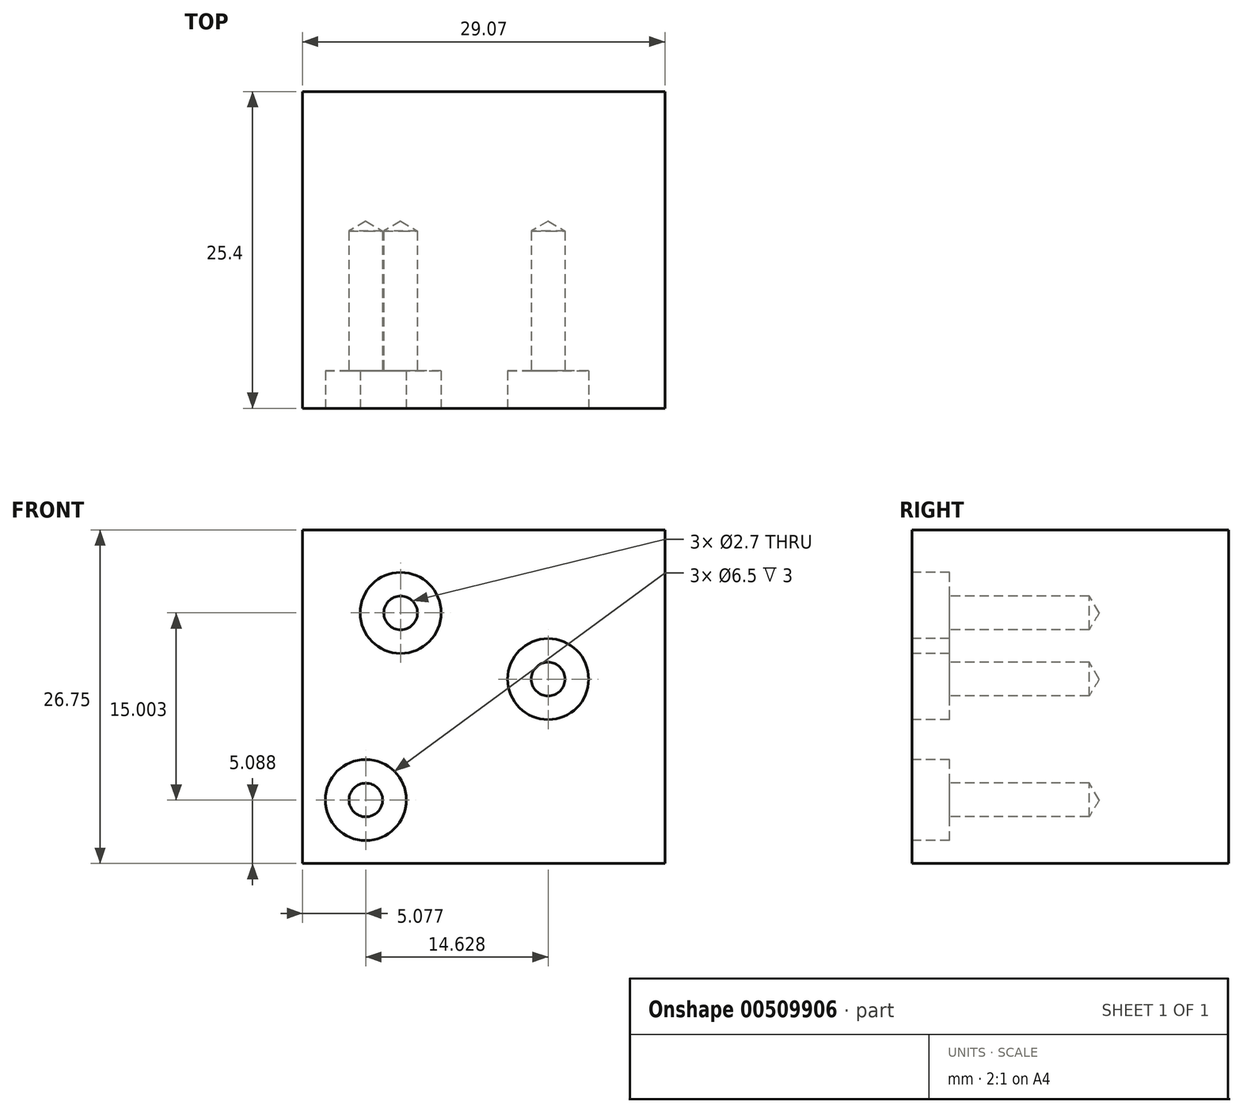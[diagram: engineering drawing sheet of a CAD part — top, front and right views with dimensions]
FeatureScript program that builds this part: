
annotation { "Feature Type Name" : "Feature", "Feature Type Description" : "" }
export const myFeature = defineFeature(function(context is Context, id is Id, definition is map)
    precondition{}
    {
        {
            var Q0;
            Q0=qCreatedBy(makeId("Front.planeOp"),FACE);
            var sketch = newSketch(context, id + "F0", { "sketchPlane" : qUnion([Q0])});
            skLineSegment(sketch, "E0.bottom", {"start": v(-46.75, 46.52) * mm, "end": v(-17.68, 46.52) * mm});
            skLineSegment(sketch, "E0.top", {"start": v(-46.75, 19.77) * mm, "end": v(-17.68, 19.77) * mm});
            skLineSegment(sketch, "E0.left", {"start": v(-46.75, 46.52) * mm, "end": v(-46.75, 19.77) * mm});
            skLineSegment(sketch, "E0.right", {"start": v(-17.68, 46.52) * mm, "end": v(-17.68, 19.77) * mm});
            skPoint(sketch, "E1", {"position": v(-38.88, 39.86) * mm});
            skPoint(sketch, "E2", {"position": v(-41.67, 24.86) * mm});
            skPoint(sketch, "E3", {"position": v(-27.04, 34.55) * mm});
            skSolve(sketch);
        }
        {
            var Q0;
            Q0=makeQuery(id+"F0.imprint","IMPRINT",FACE,{"disambiguationData":[TD([[makeQuery(id+"F0.imprint","IMPRINT",EDGE,{"derivedFrom":sQuery(id+"F0.wireOp",EDGE,"E0.bottom")}),-1.0]])]});
            extrude(context, id + "F1", {"entities" : qUnion([Q0]), "oppositeDirection" : true, "depth" : 25.4 * mm, "offsetDistance" : 25.4 * mm});
        }
        {
            var Q0;
            Q0=sQuery(id+"F0.wireOp",VERTEX,"E3");
            var Q1;
            Q1=sQuery(id+"F0.wireOp",VERTEX,"E2");
            var Q2;
            Q2=sQuery(id+"F0.wireOp",VERTEX,"E1");
            var Q3;
            Q3=makeQuery(id+"F1.opExtrude","SWEPT_BODY",BODY,{"disambiguationData":[OSD([sQuery(id+"F0.wireOp",EDGE,"E0.bottom"),sQuery(id+"F0.wireOp",EDGE,"E0.top"),sQuery(id+"F0.wireOp",EDGE,"E0.left"),sQuery(id+"F0.wireOp",EDGE,"E0.right")])]});
            hole(context, id + "F2", {"style" : HoleStyle.C_BORE, "endStyle" : HoleEndStyle.BLIND, "standardTappedOrClearance" : lookupTablePath({ "standard" : "ISO", "engagement" : "50%", "pitch" : "0.5 mm", "size" : "M3", "type" : "Tapped" }), "standardBlindInLast" : lookupTablePath({ "standard" : "ISO", "engagement" : "50%", "pitch" : "0.5 mm", "size" : "M3", "type" : "Tapped" }), "holeDiameter" : 2.7 * mm, "cBoreDiameter" : 6.5 * mm, "cBoreDepth" : 3 * mm, "showTappedDepth" : true, "holeDepth" : 14.2 * mm, "isTappedThrough" : true, "tappedDepth" : 12.7 * mm, "tapClearance" : 3, "locations" : qUnion([Q0, Q1, Q2]), "scope" : qUnion([Q3]), "majorDiameter" : 3 * mm});
        }
    });
